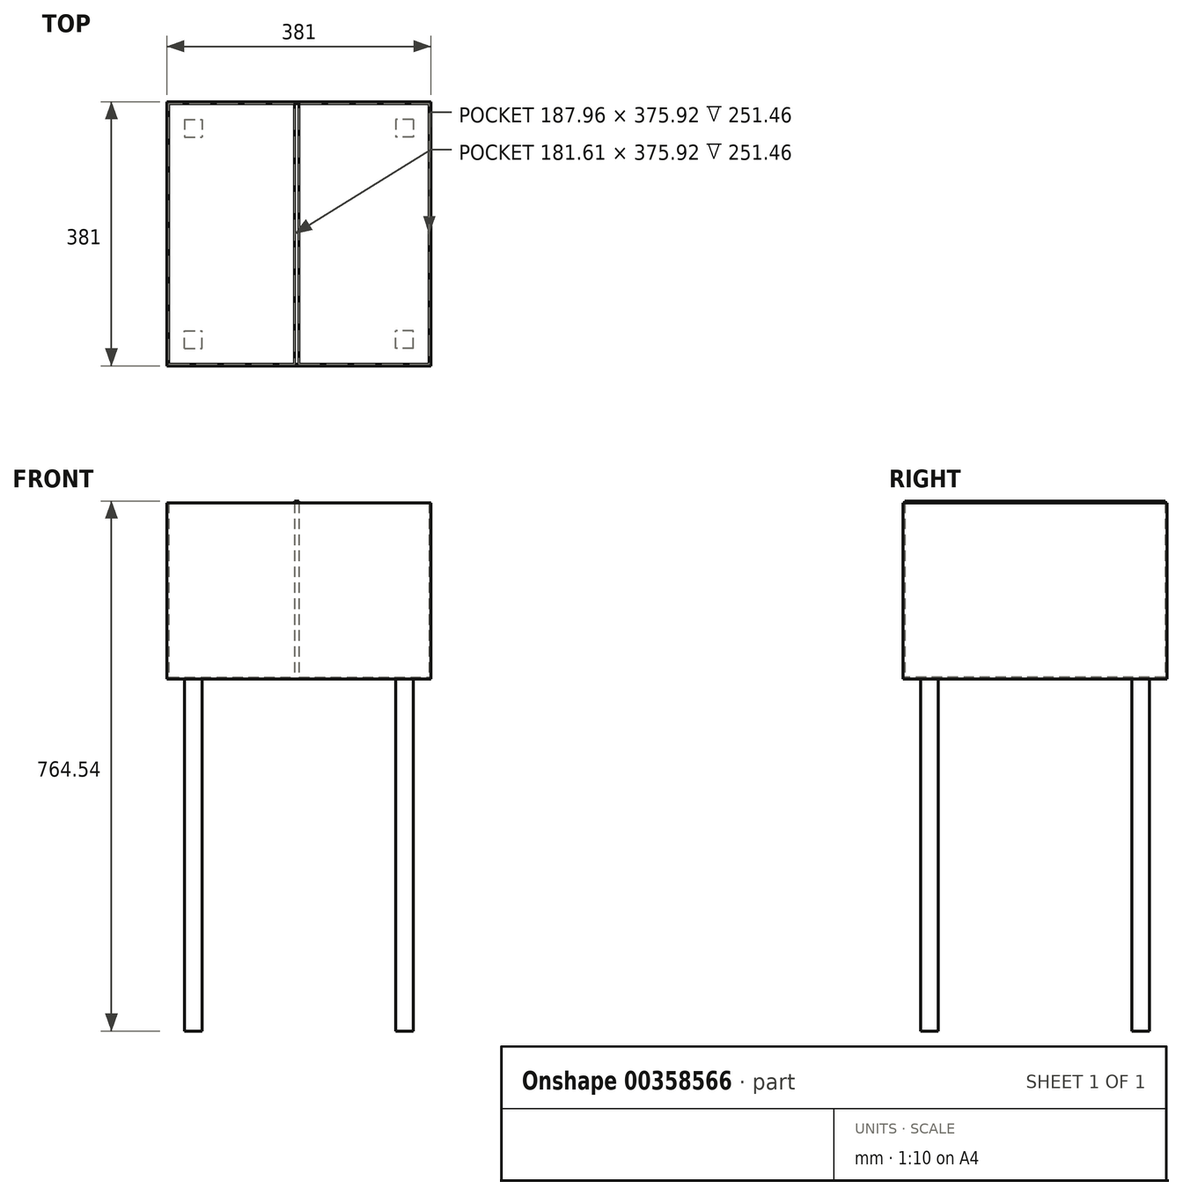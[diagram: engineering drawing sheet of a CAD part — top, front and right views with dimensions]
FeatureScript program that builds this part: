
annotation { "Feature Type Name" : "Feature", "Feature Type Description" : "" }
export const myFeature = defineFeature(function(context is Context, id is Id, definition is map)
    precondition{}
    {
        {
            var Q0;
            Q0=qCreatedBy(makeId("Top.planeOp"),FACE);
            var sketch = newSketch(context, id + "F0", { "sketchPlane" : qUnion([Q0])});
            skLineSegment(sketch, "E0.bottom", {"start": v(0, 0) * mm, "end": v(381, 0) * mm});
            skLineSegment(sketch, "E0.top", {"start": v(0, -381) * mm, "end": v(381, -381) * mm});
            skLineSegment(sketch, "E0.left", {"start": v(0, 0) * mm, "end": v(0, -381) * mm});
            skLineSegment(sketch, "E0.right", {"start": v(381, 0) * mm, "end": v(381, -381) * mm});
            skSolve(sketch);
        }
        {
            var Q0;
            Q0=qSketchRegion(id+"F0",true);
            extrude(context, id + "F1", {"entities" : qUnion([Q0]), "depth" : 254 * mm});
        }
        {
            var Q0;
            Q0=makeQuery(id+"F1.opExtrude","CAP_FACE",FACE,{"disambiguationData":[OSD([sQuery(id+"F0.wireOp",EDGE,"E0.bottom"),sQuery(id+"F0.wireOp",EDGE,"E0.top"),sQuery(id+"F0.wireOp",EDGE,"E0.left"),sQuery(id+"F0.wireOp",EDGE,"E0.right")])],"isStart":false});
            shell(context, id + "F2", {"entities" : qUnion([Q0]), "thickness" : 2.54 * mm});
        }
        {
            var Q0;
            Q0=makeQuery(id+"F1.opExtrude","CAP_FACE",FACE,{"disambiguationData":[OSD([sQuery(id+"F0.wireOp",EDGE,"E0.bottom"),sQuery(id+"F0.wireOp",EDGE,"E0.top"),sQuery(id+"F0.wireOp",EDGE,"E0.left"),sQuery(id+"F0.wireOp",EDGE,"E0.right")])],"isStart":true});
            var sketch = newSketch(context, id + "F3", { "sketchPlane" : qUnion([Q0])});
            skLineSegment(sketch, "E1.bottom", {"start": v(25.4, 355.6) * mm, "end": v(50.8, 355.6) * mm});
            skLineSegment(sketch, "E1.top", {"start": v(25.4, 330.2) * mm, "end": v(50.8, 330.2) * mm});
            skLineSegment(sketch, "E1.left", {"start": v(25.4, 355.6) * mm, "end": v(25.4, 330.2) * mm});
            skLineSegment(sketch, "E1.right", {"start": v(50.8, 355.6) * mm, "end": v(50.8, 330.2) * mm});
            skLineSegment(sketch, "E2", {"start": v(190.5, 381) * mm, "end": v(190.5, 0) * mm});
            skLineSegment(sketch, "E3", {"start": v(190.5, 0) * mm, "end": v(0, 190.5) * mm});
            skLineSegment(sketch, "E4", {"start": v(0, 190.5) * mm, "end": v(381, 190.5) * mm});
            skLineSegment(sketch, "E5.MirrorCS", {"start": v(355.6, 355.6) * mm, "end": v(330.2, 355.6) * mm});
            skLineSegment(sketch, "E6.MirrorCS", {"start": v(355.6, 330.2) * mm, "end": v(330.2, 330.2) * mm});
            skLineSegment(sketch, "E7.MirrorCS", {"start": v(355.6, 355.6) * mm, "end": v(355.6, 330.2) * mm});
            skLineSegment(sketch, "E8.MirrorCS", {"start": v(330.2, 355.6) * mm, "end": v(330.2, 330.2) * mm});
            skLineSegment(sketch, "E9.MirrorCS", {"start": v(381, 190.5) * mm, "end": v(0, 190.5) * mm});
            skLineSegment(sketch, "E10.MirrorCS", {"start": v(25.4, 25.4) * mm, "end": v(50.8, 25.4) * mm});
            skLineSegment(sketch, "E11.MirrorCS", {"start": v(25.4, 50.8) * mm, "end": v(50.8, 50.8) * mm});
            skLineSegment(sketch, "E12.MirrorCS", {"start": v(25.4, 25.4) * mm, "end": v(25.4, 50.8) * mm});
            skLineSegment(sketch, "E13.MirrorCS", {"start": v(50.8, 25.4) * mm, "end": v(50.8, 50.8) * mm});
            skLineSegment(sketch, "E14.MirrorCS", {"start": v(190.5, 0) * mm, "end": v(190.5, 381) * mm});
            skLineSegment(sketch, "E15.MirrorCS", {"start": v(330.2, 25.4) * mm, "end": v(330.2, 50.8) * mm});
            skLineSegment(sketch, "E16.MirrorCS", {"start": v(355.6, 25.4) * mm, "end": v(330.2, 25.4) * mm});
            skLineSegment(sketch, "E17.MirrorCS", {"start": v(355.6, 50.8) * mm, "end": v(330.2, 50.8) * mm});
            skLineSegment(sketch, "E18.MirrorCS", {"start": v(355.6, 25.4) * mm, "end": v(355.6, 50.8) * mm});
            skSolve(sketch);
        }
        {
            var Q0;
            Q0=makeQuery(id+"F3.imprint","IMPRINT",FACE,{"disambiguationData":[TD([[makeQuery(id+"F3.imprint","IMPRINT",EDGE,{"derivedFrom":sQuery(id+"F3.wireOp",EDGE,"E1.bottom")}),-1.0]])]});
            var Q1;
            Q1=makeQuery(id+"F3.imprint","IMPRINT",FACE,{"disambiguationData":[TD([[makeQuery(id+"F3.imprint","IMPRINT",EDGE,{"derivedFrom":sQuery(id+"F3.wireOp",EDGE,"E5.MirrorCS")}),1.0]])]});
            var Q2;
            Q2=makeQuery(id+"F3.imprint","IMPRINT",FACE,{"disambiguationData":[TD([[makeQuery(id+"F3.imprint","IMPRINT",EDGE,{"derivedFrom":sQuery(id+"F3.wireOp",EDGE,"E10.MirrorCS")}),1.0]])]});
            var Q3;
            Q3=makeQuery(id+"F3.imprint","IMPRINT",FACE,{"disambiguationData":[TD([[makeQuery(id+"F3.imprint","IMPRINT",EDGE,{"derivedFrom":sQuery(id+"F3.wireOp",EDGE,"E15.MirrorCS")}),-1.0]])]});
            extrude(context, id + "F4", {"entities" : qUnion([Q0, Q1, Q2, Q3]), "operationType" : NewBodyOperationType.ADD, "depth" : 508 * mm});
        }
        {
            var Q0;
            Q0=makeQuery(id+"F2.opShell","OFFSET_FACE",FACE,{"disambiguationData":[OSD([sQuery(id+"F0.wireOp",EDGE,"E0.bottom"),sQuery(id+"F0.wireOp",EDGE,"E0.top"),sQuery(id+"F0.wireOp",EDGE,"E0.left"),sQuery(id+"F0.wireOp",EDGE,"E0.right")])]});
            var sketch = newSketch(context, id + "F5", { "sketchPlane" : qUnion([Q0])});
            skLineSegment(sketch, "E19.bottom", {"start": v(190.5, -2.54) * mm, "end": v(184.15, -2.54) * mm});
            skLineSegment(sketch, "E19.top", {"start": v(190.5, -378.46) * mm, "end": v(184.15, -378.46) * mm});
            skLineSegment(sketch, "E19.left", {"start": v(190.5, -2.54) * mm, "end": v(190.5, -378.46) * mm});
            skLineSegment(sketch, "E19.right", {"start": v(184.15, -2.54) * mm, "end": v(184.15, -378.46) * mm});
            skSolve(sketch);
        }
        {
            var Q0;
            Q0=makeQuery(id+"F5.imprint","IMPRINT",FACE,{"disambiguationData":[TD([[makeQuery(id+"F5.imprint","IMPRINT",EDGE,{"derivedFrom":sQuery(id+"F5.wireOp",EDGE,"E19.bottom")}),-1.0]])]});
            extrude(context, id + "F6", {"entities" : qUnion([Q0]), "operationType" : NewBodyOperationType.ADD, "depth" : 254 * mm});
        }
    });
